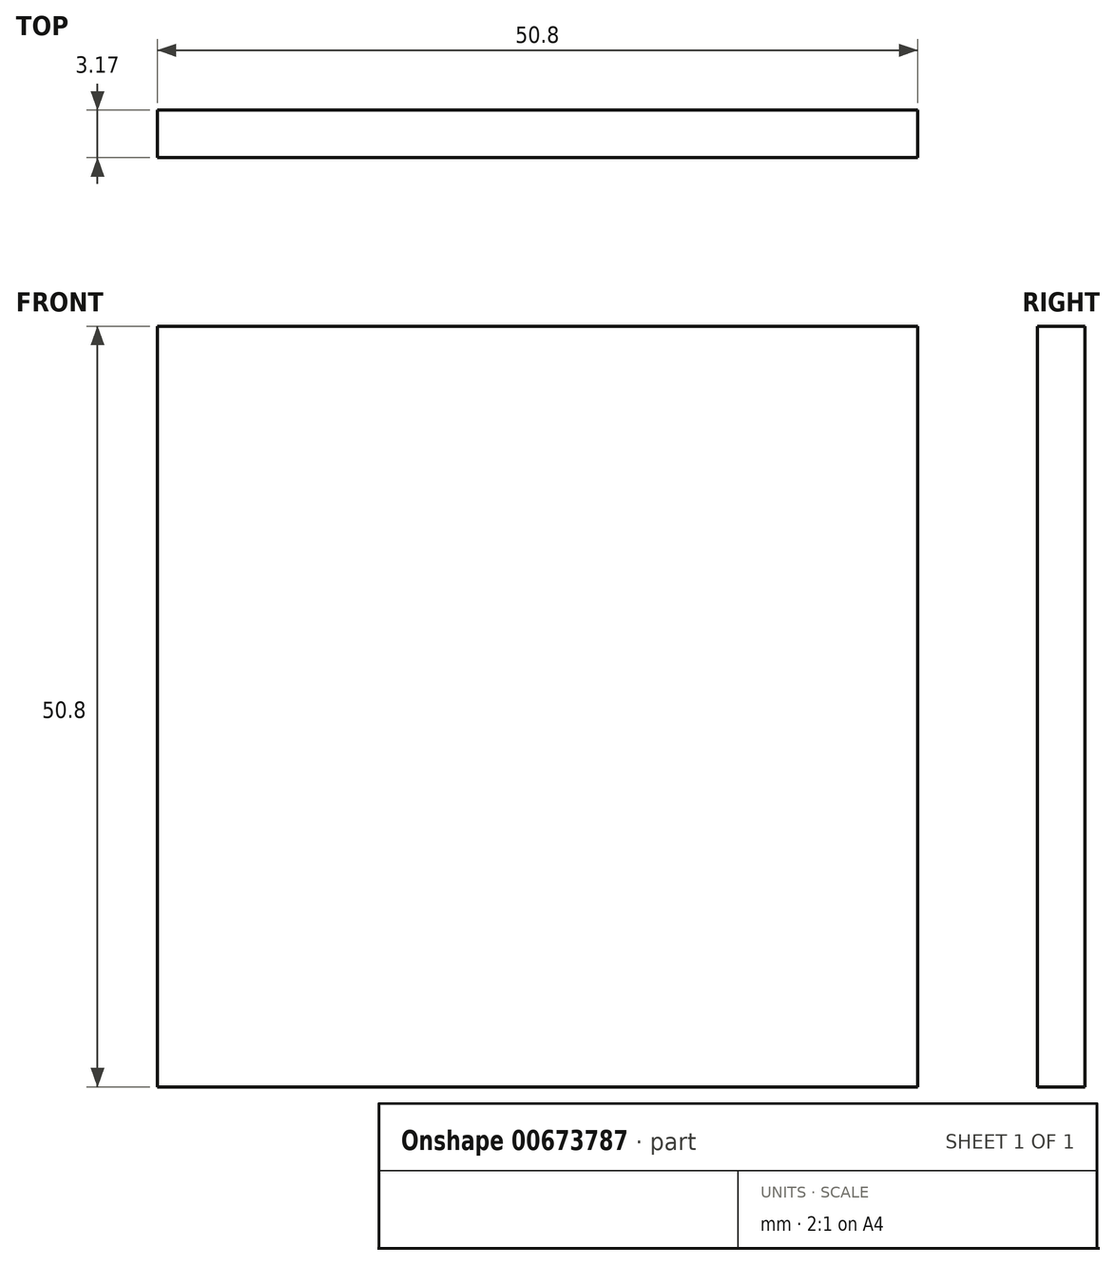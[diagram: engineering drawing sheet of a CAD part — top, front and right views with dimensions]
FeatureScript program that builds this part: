
annotation { "Feature Type Name" : "Feature", "Feature Type Description" : "" }
export const myFeature = defineFeature(function(context is Context, id is Id, definition is map)
    precondition{}
    {
        {
            var Q0;
            Q0=qCreatedBy(makeId("Front.planeOp"),FACE);
            var sketch = newSketch(context, id + "F0", { "sketchPlane" : qUnion([Q0])});
            skLineSegment(sketch, "E0.bottom", {"start": v(25.4, 25.4) * mm, "end": v(-25.4, 25.4) * mm});
            skLineSegment(sketch, "E0.top", {"start": v(25.4, -25.4) * mm, "end": v(-25.4, -25.4) * mm});
            skLineSegment(sketch, "E0.left", {"start": v(25.4, 25.4) * mm, "end": v(25.4, -25.4) * mm});
            skLineSegment(sketch, "E0.right", {"start": v(-25.4, 25.4) * mm, "end": v(-25.4, -25.4) * mm});
            skPoint(sketch, "E0.middle", {"position": v(0, 0) * mm});
            skSolve(sketch);
        }
        {
            var Q0;
            Q0 = qSketchRegion(id + "F0", true);
            extrude(context, id + "F1", {"entities" : qUnion([Q0]), "depth" : 3.17 * mm, "offsetDistance" : 25.4 * mm});
        }
    });
